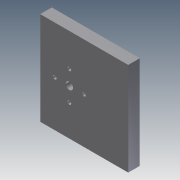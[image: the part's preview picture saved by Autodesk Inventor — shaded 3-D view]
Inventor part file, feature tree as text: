
AUTODESK INVENTOR PART (.ipt)
format: ipt  version: 2011 (Build 150239000, 239)  size: 116,736 bytes
history: native  units: in
note: dims shown in document units (in); Inventor stores cm internally (conversion verified against a paired STEP export)
features: extrude x5, sketch x5
ambient origin geometry x8: Origin, YZ Plane, XZ Plane, XY Plane, X Axis, Y Axis, Z Axis, Center Point
bodies: Solid1 (feature_tree)
feature tree (10):
  extrude  "Extrusion1"  Depth=2.0079in
  extrude  "Extrusion2"  Depth=0.9843in
  extrude  "Extrusion3"  Depth=0.0787in
  extrude  "Extrusion4"  Depth=0.0787in
  extrude  "Extrusion5"  Depth=0.6299in
  sketch  "Sketch1"  dims[d0=1.7717in d1=2.0079in]
  sketch  "Sketch2"  dims[d2=0.125in d3=0.0in d4=0.9843in]
  sketch  "Sketch3"  dims[d6=0.6299in d7=0.0787in]
  sketch  "Sketch4"  dims[d8=0.0787in d9=0.0787in]
  sketch  "Sketch5"  dims[d10=0.0787in d11=0.6299in d12=1.0in d13=0.0in d14=0.156in d15=1.0in d16=0.0in d17=0.25in d18=0.125in d19=0.0in d20=0.125in d21=0.0in]
